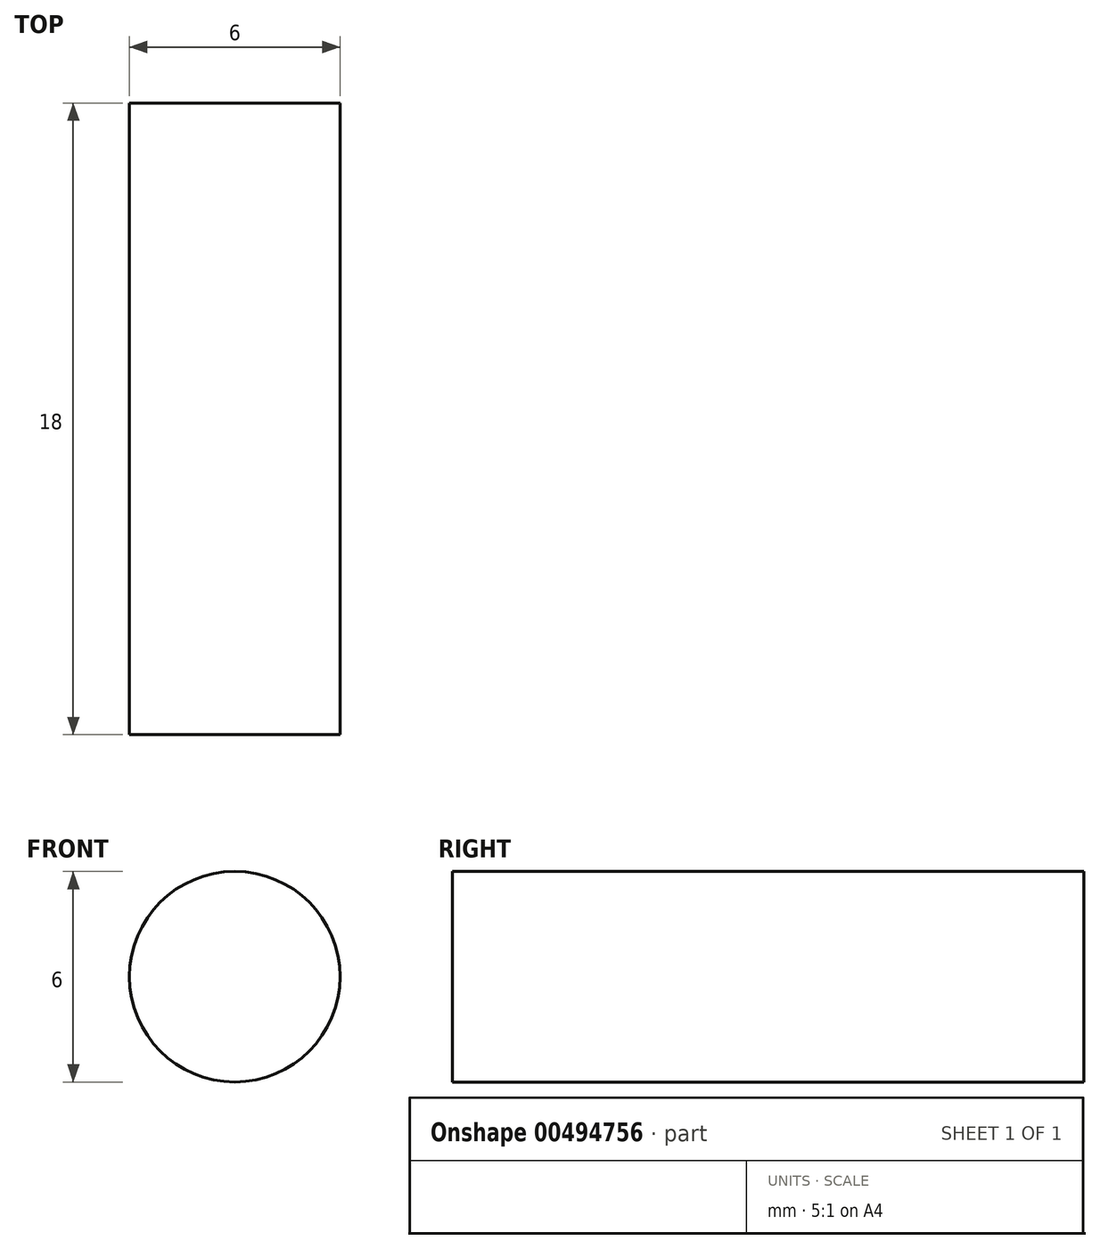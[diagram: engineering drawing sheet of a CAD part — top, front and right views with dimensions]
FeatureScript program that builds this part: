
annotation { "Feature Type Name" : "Feature", "Feature Type Description" : "" }
export const myFeature = defineFeature(function(context is Context, id is Id, definition is map)
    precondition{}
    {
        {
            var Q0;
            Q0=qCreatedBy(makeId("Front.planeOp"),FACE);
            var sketch = newSketch(context, id + "F0", { "sketchPlane" : qUnion([Q0])});
            skCircle(sketch, "E0", {"center": v(0, 0) * mm, "radius": 3 * mm});
            skSolve(sketch);
        }
        {
            var Q0;
            Q0 = qSketchRegion(id + "F0", true);
            extrude(context, id + "F1", {"entities" : qUnion([Q0]), "depth" : 18 * mm});
        }
    });
